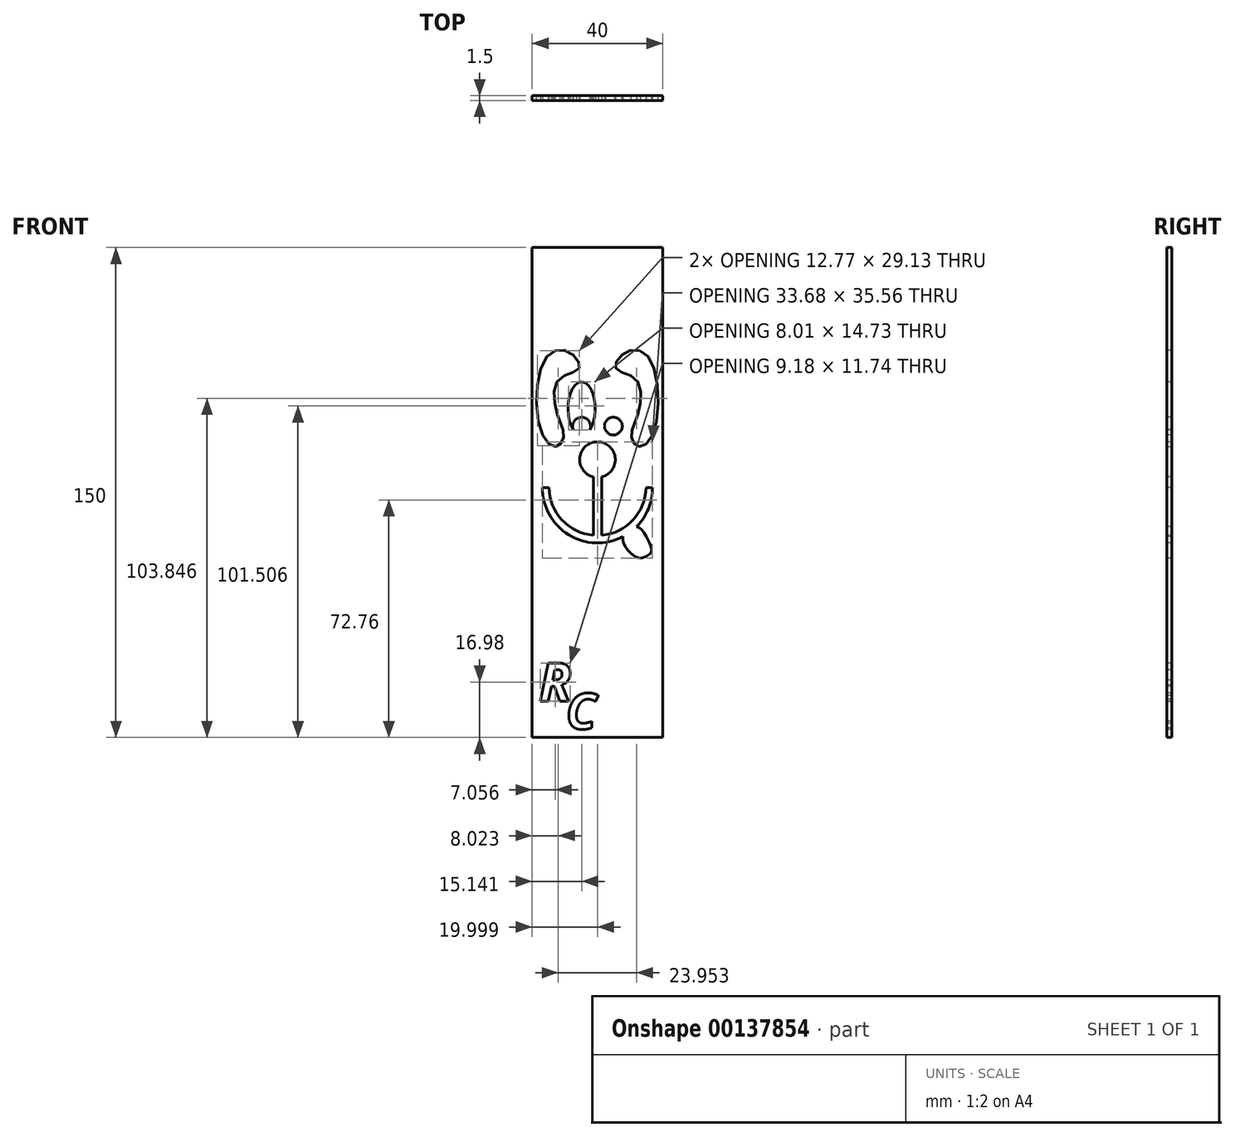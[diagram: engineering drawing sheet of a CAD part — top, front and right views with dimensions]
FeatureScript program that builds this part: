
annotation { "Feature Type Name" : "Feature", "Feature Type Description" : "" }
export const myFeature = defineFeature(function(context is Context, id is Id, definition is map)
    precondition{}
    {
        {
            var Q0;
            Q0=qCreatedBy(makeId("Front.planeOp"),FACE);
            var sketch = newSketch(context, id + "F0", { "sketchPlane" : qUnion([Q0])});
            skLineSegment(sketch, "E0", {"start": v(0, 73.44) * mm, "end": v(0, -76.56) * mm});
            skLineSegment(sketch, "E1", {"start": v(0, 73.44) * mm, "end": v(-40, 73.44) * mm});
            skLineSegment(sketch, "E2", {"start": v(-40, 73.44) * mm, "end": v(-40, -76.56) * mm});
            skLineSegment(sketch, "E3", {"start": v(-40, -76.56) * mm, "end": v(0, -76.56) * mm});
            skSolve(sketch);
        }
        {
            var Q0;
            Q0 = qSketchRegion(id + "F0", true);
            extrude(context, id + "F1", {"entities" : qUnion([Q0]), "depth" : 1.5 * mm});
        }
        {
            var Q0;
            Q0=makeQuery(id+"F1.opExtrude","CAP_FACE",FACE,{"disambiguationData":[OSD([sQuery(id+"F0.wireOp",EDGE,"E0"),sQuery(id+"F0.wireOp",EDGE,"E1"),sQuery(id+"F0.wireOp",EDGE,"E2"),sQuery(id+"F0.wireOp",EDGE,"E3")])],"isStart":false});
            var sketch = newSketch(context, id + "F2", { "sketchPlane" : qUnion([Q0])});
            skLineSegment(sketch, "E4", {"start": v(-20, 73.44) * mm, "end": v(-20, -76.56) * mm});
            skLineSegment(sketch, "E5", {"start": v(-40, 73.44) * mm, "end": v(-20, 73.44) * mm});
            skEllipse(sketch, "E6", {"center": v(-24.85, 24.17) * mm, "majorRadius": 8.14 * mm, "minorRadius": 4.19 * mm, "majorAxis": v(0, -1)});
            skEllipse(sketch, "E7.MirrorC", {"center": v(-15.15, 24.17) * mm, "majorRadius": 8.14 * mm, "minorRadius": 4.19 * mm, "majorAxis": v(0, -1)});
            skCircle(sketch, "E8", {"center": v(-20, 8.54) * mm, "radius": 5.44 * mm});
            skArc(sketch, "E9", {"start": v(-34.84, 0) * mm, "mid": v(-20, -14.7) * mm, "end": v(-5.16, 0) * mm});
            skArc(sketch, "E10", {"start": v(-36.84, 0) * mm, "mid": v(-20, -16.98) * mm, "end": v(-3.16, 0) * mm});
            skLineSegment(sketch, "E11", {"start": v(-21.25, 3.24) * mm, "end": v(-21.25, -14.65) * mm});
            skLineSegment(sketch, "E12.MirrorCS", {"start": v(-18.75, 3.24) * mm, "end": v(-18.75, -14.65) * mm});
            skLineSegment(sketch, "E13", {"start": v(-36.84, 0) * mm, "end": v(-34.84, 0) * mm});
            skLineSegment(sketch, "E14", {"start": v(-5.16, 0) * mm, "end": v(-3.16, 0) * mm});
            skFitSpline(sketch, "E15", {"points": [v(-14.4, 36.49) * mm, v(-11.57, 41.28) * mm, v(-4.11, 39.5) * mm, v(-3.4, 15.55) * mm, v(-8.02, 12.75) * mm, v(-9.62, 16.44) * mm, v(-7.66, 22.3) * mm, v(-8.2, 33.12) * mm, v(-14.4, 36.49) * mm]});
            skFitSpline(sketch, "E16.MirrorC", {"points": [v(-25.6, 36.49) * mm, v(-28.43, 41.28) * mm, v(-35.89, 39.5) * mm, v(-36.6, 15.55) * mm, v(-31.98, 12.75) * mm, v(-30.38, 16.44) * mm, v(-32.34, 22.3) * mm, v(-31.8, 33.12) * mm, v(-25.6, 36.49) * mm]});
            skArc(sketch, "E17", {"start": v(-22.39, 17.58) * mm, "mid": v(-24.77, 21.49) * mm, "end": v(-27.42, 17.75) * mm});
            skArc(sketch, "E18.MirrorCS", {"start": v(-17.61, 17.58) * mm, "mid": v(-15.23, 21.49) * mm, "end": v(-12.58, 17.75) * mm});
            skFitSpline(sketch, "E19", {"points": [v(-12.2, -15.07) * mm, v(-9.44, -20.47) * mm, v(-6.24, -21.53) * mm, v(-3.58, -19.76) * mm, v(-4.47, -16.2) * mm, v(-8.02, -11.98) * mm, v(-12.2, -15.07) * mm]});
            skSolve(sketch);
        }
        {
            var Q0;
            {var subQ0=sQuery(id+"F2.wireOp",EDGE,"E17");Q0=makeQuery(id+"F2.imprint","IMPRINT",FACE,{"disambiguationData":[TD([[makeQuery(id+"F2.imprint","IMPRINT",EDGE,{"derivedFrom":subQ0}),-1.0]])]});}
            var Q1;
            Q1=makeQuery(id+"F2.imprint","IMPRINT",FACE,{"disambiguationData":[TD([[makeQuery(id+"F2.imprint","IMPRINT",EDGE,{"derivedFrom":sQuery(id+"F2.wireOp",EDGE,"E16.MirrorC")}),1.0]])]});
            var Q2;
            {var subQ0=sQuery(id+"F2.wireOp",EDGE,"E18.MirrorCS");Q2=makeQuery(id+"F2.imprint","IMPRINT",FACE,{"disambiguationData":[TD([[makeQuery(id+"F2.imprint","IMPRINT",EDGE,{"derivedFrom":subQ0}),1.0]])]});}
            var Q3;
            Q3=makeQuery(id+"F2.imprint","IMPRINT",FACE,{"disambiguationData":[TD([[makeQuery(id+"F2.imprint","IMPRINT",EDGE,{"derivedFrom":sQuery(id+"F2.wireOp",EDGE,"E15")}),-1.0]])]});
            var Q4;
            {var subQ0=sQuery(id+"F2.wireOp",EDGE,"E8");var subQ1=sQuery(id+"F2.wireOp",EDGE,"E4");var subQ2=makeQuery(id+"F2.imprint","INTERSECT",VERTEX,{"disambiguationData":[OD(0.0)],"derivedFrom":[subQ1,subQ0]});Q4=makeQuery(id+"F2.imprint","IMPRINT",FACE,{"disambiguationData":[TD([[makeQuery(id+"F2.imprint","IMPRINT",EDGE,{"disambiguationData":[TD([[subQ2,-1.0]])],"derivedFrom":subQ1}),-1.0]])]});}
            var Q5;
            {var subQ0=sQuery(id+"F2.wireOp",EDGE,"E8");var subQ1=sQuery(id+"F2.wireOp",EDGE,"E4");var subQ2=makeQuery(id+"F2.imprint","INTERSECT",VERTEX,{"disambiguationData":[OD(0.0)],"derivedFrom":[subQ1,subQ0]});Q5=makeQuery(id+"F2.imprint","IMPRINT",FACE,{"disambiguationData":[TD([[makeQuery(id+"F2.imprint","IMPRINT",EDGE,{"disambiguationData":[TD([[subQ2,-1.0]])],"derivedFrom":subQ1}),1.0]])]});}
            var Q6;
            {var subQ5=sQuery(id+"F2.wireOp",EDGE,"E11");Q6=makeQuery(id+"F2.imprint","IMPRINT",FACE,{"disambiguationData":[TD([[makeQuery(id+"F2.imprint","IMPRINT",EDGE,{"derivedFrom":subQ5}),1.0]])]});}
            var Q7;
            {var subQ5=sQuery(id+"F2.wireOp",EDGE,"E12.MirrorCS");Q7=makeQuery(id+"F2.imprint","IMPRINT",FACE,{"disambiguationData":[TD([[makeQuery(id+"F2.imprint","IMPRINT",EDGE,{"derivedFrom":subQ5}),-1.0]])]});}
            var Q8;
            {var subQ7=sQuery(id+"F2.wireOp",EDGE,"E14");Q8=makeQuery(id+"F2.imprint","IMPRINT",FACE,{"disambiguationData":[TD([[makeQuery(id+"F2.imprint","IMPRINT",EDGE,{"derivedFrom":subQ7}),-1.0]])]});}
            var Q9;
            {var subQ4=sQuery(id+"F2.wireOp",EDGE,"E13");Q9=makeQuery(id+"F2.imprint","IMPRINT",FACE,{"disambiguationData":[TD([[makeQuery(id+"F2.imprint","IMPRINT",EDGE,{"derivedFrom":subQ4}),-1.0]])]});}
            var Q10;
            {var subQ0=sQuery(id+"F2.wireOp",EDGE,"E19");var subQ1=sQuery(id+"F2.wireOp",EDGE,"E10");var subQ2=makeQuery(id+"F2.imprint","INTERSECT",VERTEX,{"disambiguationData":[OD(0.0)],"derivedFrom":[subQ1,subQ0]});Q10=makeQuery(id+"F2.imprint","IMPRINT",FACE,{"disambiguationData":[TD([[makeQuery(id+"F2.imprint","IMPRINT",EDGE,{"disambiguationData":[TD([[subQ2,-1.0]])],"derivedFrom":subQ1}),-1.0]])]});}
            var Q11;
            {var subQ0=sQuery(id+"F2.wireOp",EDGE,"E19");var subQ1=sQuery(id+"F2.wireOp",EDGE,"E10");var subQ2=makeQuery(id+"F2.imprint","INTERSECT",VERTEX,{"disambiguationData":[OD(0.0)],"derivedFrom":[subQ1,subQ0]});Q11=makeQuery(id+"F2.imprint","IMPRINT",FACE,{"disambiguationData":[TD([[makeQuery(id+"F2.imprint","IMPRINT",EDGE,{"disambiguationData":[TD([[subQ2,-1.0]])],"derivedFrom":subQ1}),1.0]])]});}
            extrude(context, id + "F3", {"entities" : qUnion([Q0, Q1, Q2, Q3, Q4, Q5, Q6, Q7, Q8, Q9, Q10, Q11]), "operationType" : NewBodyOperationType.REMOVE, "oppositeDirection" : true, "depth" : 25 * mm});
        }
        {
            var Q0;
            Q0=makeQuery(id+"F1.opExtrude","CAP_FACE",FACE,{"disambiguationData":[OSD([sQuery(id+"F0.wireOp",EDGE,"E0"),sQuery(id+"F0.wireOp",EDGE,"E1"),sQuery(id+"F0.wireOp",EDGE,"E2"),sQuery(id+"F0.wireOp",EDGE,"E3")])],"isStart":false});
            var sketch = newSketch(context, id + "F4", { "sketchPlane" : qUnion([Q0])});
            skText(sketch, "E20", { "text": "C", "fontName": "OpenSans-BoldItalic.ttf"});
            skPoint(sketch, "E20.firstSnap0", {"position": v(-27.73, -62.96) * mm});
            skText(sketch, "E21", { "text": "R", "fontName": "OpenSans-BoldItalic.ttf"});
            const initialGuessF4  = {"E20": [-0.02968, -0.07398, 1, 0, 0.01101], "E21": [-0.03796, -0.06545, 1, 0, 0.01184]};
            skSetInitialGuess(sketch, initialGuessF4);
            skSolve(sketch);
        }
        {
            var Q0;
            Q0 = qSketchRegion(id + "F4", true);
            extrude(context, id + "F5", {"entities" : qUnion([Q0]), "operationType" : NewBodyOperationType.REMOVE, "oppositeDirection" : true, "depth" : 25 * mm});
        }
    });
